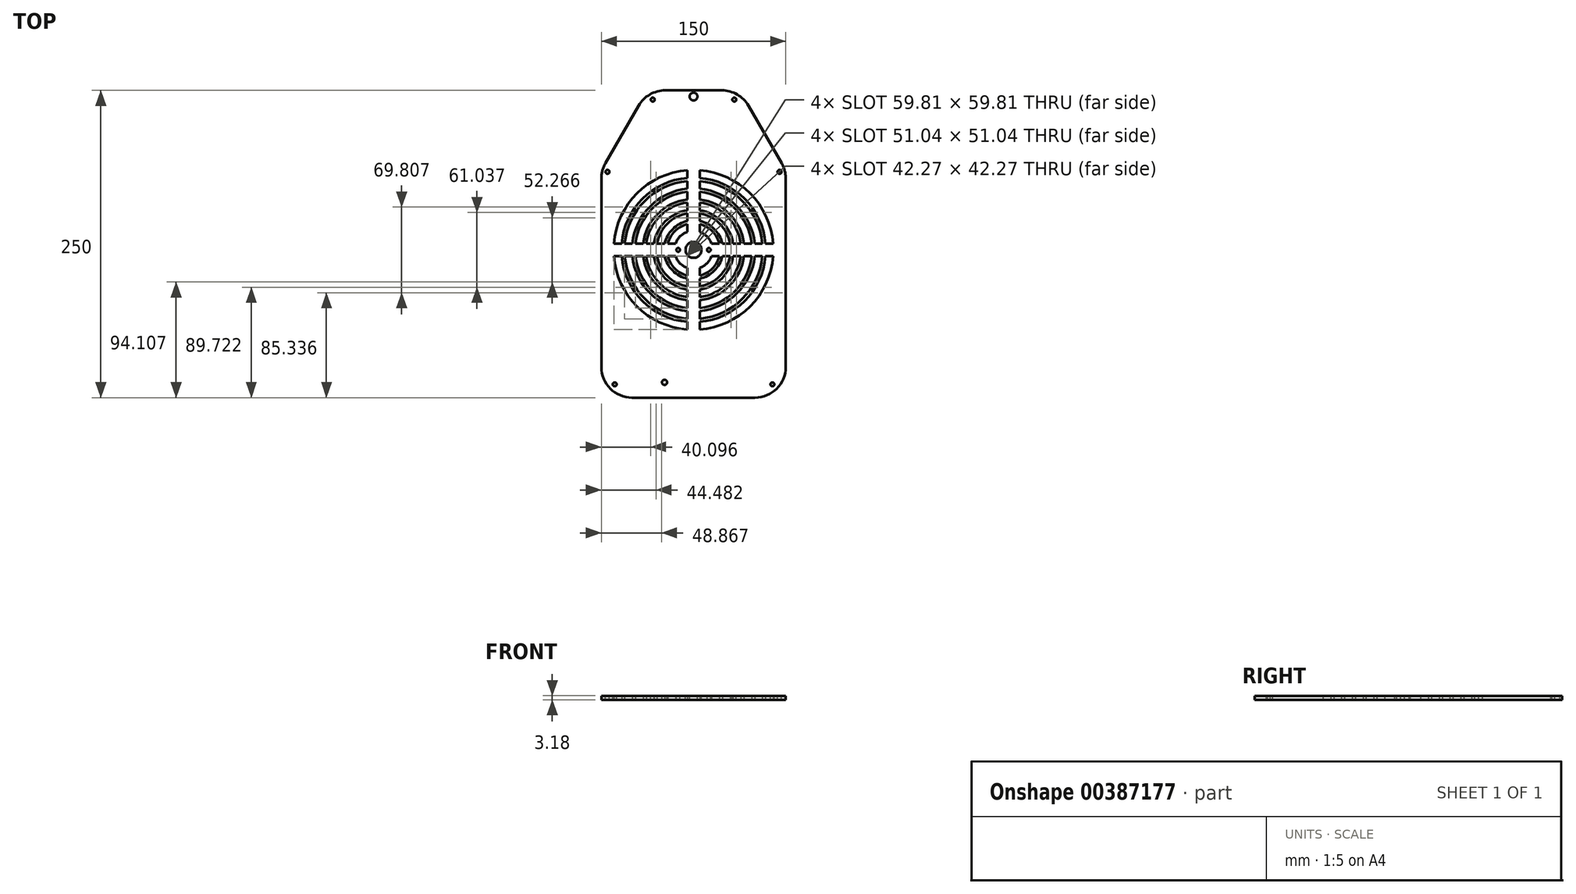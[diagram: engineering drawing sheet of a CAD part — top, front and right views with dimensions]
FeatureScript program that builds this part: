
annotation { "Feature Type Name" : "Feature", "Feature Type Description" : "" }
export const myFeature = defineFeature(function(context is Context, id is Id, definition is map)
    precondition{}
    {
        {
            var Q0;
            Q0=qCreatedBy(makeId("Top.planeOp"),FACE);
            var sketch = newSketch(context, id + "F0", { "sketchPlane" : qUnion([Q0])});
            skLineSegment(sketch, "E0", {"start": v(-75, -120.24) * mm, "end": v(75, -120.24) * mm});
            skLineSegment(sketch, "E1", {"start": v(75, -120.24) * mm, "end": v(75, 64.8) * mm});
            skLineSegment(sketch, "E2", {"start": v(75, 64.8) * mm, "end": v(37.5, 129.76) * mm});
            skLineSegment(sketch, "E3", {"start": v(37.5, 129.76) * mm, "end": v(-37.5, 129.76) * mm});
            skLineSegment(sketch, "E4", {"start": v(-37.5, 129.76) * mm, "end": v(-75, 64.8) * mm});
            skLineSegment(sketch, "E5", {"start": v(-75, 64.8) * mm, "end": v(-75, -120.24) * mm});
            skArc(sketch, "E6", {"start": v(-5, 64.8) * mm, "mid": v(-45.96, 45.96) * mm, "end": v(-64.8, 5) * mm});
            skLineSegment(sketch, "E7", {"start": v(-5, 64.8) * mm, "end": v(-5, 58.54) * mm});
            skLineSegment(sketch, "E8", {"start": v(-23.45, 5) * mm, "end": v(-29.73, 5) * mm});
            skLineSegment(sketch, "E9", {"start": v(-64.8, -5) * mm, "end": v(-58.54, -5) * mm});
            skLineSegment(sketch, "E10", {"start": v(-5, -23.45) * mm, "end": v(-5, -29.73) * mm});
            skLineSegment(sketch, "E11", {"start": v(5, -64.8) * mm, "end": v(5, -58.54) * mm});
            skLineSegment(sketch, "E12", {"start": v(23.45, -5) * mm, "end": v(29.73, -5) * mm});
            skLineSegment(sketch, "E13", {"start": v(64.8, 5) * mm, "end": v(58.54, 5) * mm});
            skLineSegment(sketch, "E14", {"start": v(5, 23.45) * mm, "end": v(5, 29.73) * mm});
            skArc(sketch, "E15.trimOffspring", {"start": v(64.8, 5) * mm, "mid": v(45.96, 45.96) * mm, "end": v(5, 64.8) * mm});
            skArc(sketch, "E16.trimOffspring", {"start": v(5, -64.8) * mm, "mid": v(45.96, -45.96) * mm, "end": v(64.8, -5) * mm});
            skArc(sketch, "E17.trimOffspring", {"start": v(-64.8, -5) * mm, "mid": v(-45.96, -45.96) * mm, "end": v(-5, -64.8) * mm});
            skPoint(sketch, "E18.visualSharp", {"position": v(-75, -120.24) * mm});
            skPoint(sketch, "E19.visualSharp", {"position": v(75, -120.24) * mm});
            skArc(sketch, "E20", {"start": v(-5, 23.45) * mm, "mid": v(-16.96, 16.96) * mm, "end": v(-23.45, 5) * mm});
            skArc(sketch, "E21.trimOffspring", {"start": v(-23.45, -5) * mm, "mid": v(-16.96, -16.96) * mm, "end": v(-5, -23.45) * mm});
            skArc(sketch, "E22.trimOffspring", {"start": v(23.45, 5) * mm, "mid": v(16.96, 16.96) * mm, "end": v(5, 23.45) * mm});
            skArc(sketch, "E23.trimOffspring", {"start": v(5, -23.45) * mm, "mid": v(16.96, -16.96) * mm, "end": v(23.45, -5) * mm});
            skLineSegment(sketch, "E24", {"start": v(0, 129.76) * mm, "end": v(0, -120.24) * mm, "construction": true});
            skArc(sketch, "E25", {"start": v(58.54, 5) * mm, "mid": v(41.54, 41.54) * mm, "end": v(5, 58.54) * mm});
            skArc(sketch, "E26", {"start": v(-56.04, -5) * mm, "mid": v(-39.78, -39.78) * mm, "end": v(-5, -56.04) * mm});
            skArc(sketch, "E27", {"start": v(-5, 49.77) * mm, "mid": v(-35.37, 35.37) * mm, "end": v(-49.77, 5) * mm});
            skArc(sketch, "E28", {"start": v(-5, 47.27) * mm, "mid": v(-33.6, 33.6) * mm, "end": v(-47.27, 5) * mm});
            skLineSegment(sketch, "E29.trimOffspring", {"start": v(-5, 56.04) * mm, "end": v(-5, 49.77) * mm});
            skLineSegment(sketch, "E30.trimOffspring", {"start": v(5, 58.54) * mm, "end": v(5, 64.8) * mm});
            skLineSegment(sketch, "E31.trimOffspring", {"start": v(-58.54, 5) * mm, "end": v(-64.8, 5) * mm});
            skLineSegment(sketch, "E32.trimOffspring", {"start": v(-56.04, -5) * mm, "end": v(-49.77, -5) * mm});
            skLineSegment(sketch, "E33.trimOffspring", {"start": v(-5, -58.54) * mm, "end": v(-5, -64.8) * mm});
            skLineSegment(sketch, "E34.trimOffspring", {"start": v(5, -56.04) * mm, "end": v(5, -49.77) * mm});
            skLineSegment(sketch, "E35.trimOffspring", {"start": v(58.54, -5) * mm, "end": v(64.8, -5) * mm});
            skLineSegment(sketch, "E36.trimOffspring", {"start": v(56.04, 5) * mm, "end": v(49.77, 5) * mm});
            skArc(sketch, "E37.trimOffspring", {"start": v(-58.54, -5) * mm, "mid": v(-41.54, -41.54) * mm, "end": v(-5, -58.54) * mm});
            skArc(sketch, "E38.trimOffspring", {"start": v(-5, 58.54) * mm, "mid": v(-41.54, 41.54) * mm, "end": v(-58.54, 5) * mm});
            skArc(sketch, "E39.trimOffspring", {"start": v(-5, 56.04) * mm, "mid": v(-39.78, 39.78) * mm, "end": v(-56.04, 5) * mm});
            skLineSegment(sketch, "E40.trimOffspring", {"start": v(-5, 47.27) * mm, "end": v(-5, 41) * mm});
            skLineSegment(sketch, "E41.trimOffspring", {"start": v(-49.77, 5) * mm, "end": v(-56.04, 5) * mm});
            skArc(sketch, "E42.trimOffspring", {"start": v(-49.77, -5) * mm, "mid": v(-35.37, -35.37) * mm, "end": v(-5, -49.77) * mm});
            skArc(sketch, "E43.trimOffspring", {"start": v(-47.27, -5) * mm, "mid": v(-33.6, -33.6) * mm, "end": v(-5, -47.27) * mm});
            skLineSegment(sketch, "E44.trimOffspring", {"start": v(-47.27, -5) * mm, "end": v(-41, -5) * mm});
            skLineSegment(sketch, "E45.trimOffspring", {"start": v(47.27, 5) * mm, "end": v(41, 5) * mm});
            skArc(sketch, "E46.trimOffspring", {"start": v(49.77, 5) * mm, "mid": v(35.37, 35.37) * mm, "end": v(5, 49.77) * mm});
            skArc(sketch, "E47.trimOffspring", {"start": v(47.27, 5) * mm, "mid": v(33.6, 33.6) * mm, "end": v(5, 47.27) * mm});
            skArc(sketch, "E48.trimOffspring", {"start": v(56.04, 5) * mm, "mid": v(39.78, 39.78) * mm, "end": v(5, 56.04) * mm});
            skLineSegment(sketch, "E49.trimOffspring", {"start": v(-5, -49.77) * mm, "end": v(-5, -56.04) * mm});
            skArc(sketch, "E50.trimOffspring", {"start": v(5, -47.27) * mm, "mid": v(33.6, -33.6) * mm, "end": v(47.27, -5) * mm});
            skArc(sketch, "E51.trimOffspring", {"start": v(5, -49.77) * mm, "mid": v(35.37, -35.37) * mm, "end": v(49.77, -5) * mm});
            skArc(sketch, "E52.trimOffspring", {"start": v(5, -56.04) * mm, "mid": v(39.78, -39.78) * mm, "end": v(56.04, -5) * mm});
            skLineSegment(sketch, "E53.trimOffspring", {"start": v(5, -47.27) * mm, "end": v(5, -41) * mm});
            skArc(sketch, "E54.trimOffspring", {"start": v(5, -58.54) * mm, "mid": v(41.54, -41.54) * mm, "end": v(58.54, -5) * mm});
            skLineSegment(sketch, "E55.trimOffspring", {"start": v(49.77, -5) * mm, "end": v(56.04, -5) * mm});
            skLineSegment(sketch, "E56.trimOffspring", {"start": v(5, 49.77) * mm, "end": v(5, 56.04) * mm});
            skArc(sketch, "E57", {"start": v(-5, 41) * mm, "mid": v(-29.2, 29.2) * mm, "end": v(-41, 5) * mm});
            skArc(sketch, "E58", {"start": v(-5, 29.73) * mm, "mid": v(-21.31, 21.31) * mm, "end": v(-29.73, 5) * mm});
            skArc(sketch, "E59.trimOffspring", {"start": v(-29.73, -5) * mm, "mid": v(-21.31, -21.31) * mm, "end": v(-5, -29.73) * mm});
            skArc(sketch, "E60.trimOffspring", {"start": v(-41, -5) * mm, "mid": v(-29.2, -29.2) * mm, "end": v(-5, -41) * mm});
            skArc(sketch, "E61.trimOffspring", {"start": v(5, -29.73) * mm, "mid": v(21.31, -21.31) * mm, "end": v(29.73, -5) * mm});
            skArc(sketch, "E62.trimOffspring", {"start": v(5, -41) * mm, "mid": v(29.2, -29.2) * mm, "end": v(41, -5) * mm});
            skArc(sketch, "E63.trimOffspring", {"start": v(29.73, 5) * mm, "mid": v(21.31, 21.31) * mm, "end": v(5, 29.73) * mm});
            skArc(sketch, "E64.trimOffspring", {"start": v(41, 5) * mm, "mid": v(29.2, 29.2) * mm, "end": v(5, 41) * mm});
            skLineSegment(sketch, "E65.trimOffspring", {"start": v(-5, 29.73) * mm, "end": v(-5, 23.45) * mm});
            skLineSegment(sketch, "E66.trimOffspring", {"start": v(5, 41) * mm, "end": v(5, 47.27) * mm});
            skLineSegment(sketch, "E67.trimOffspring", {"start": v(29.73, 5) * mm, "end": v(23.45, 5) * mm});
            skLineSegment(sketch, "E68.trimOffspring", {"start": v(41, -5) * mm, "end": v(47.27, -5) * mm});
            skLineSegment(sketch, "E69.trimOffspring", {"start": v(5, -29.73) * mm, "end": v(5, -23.45) * mm});
            skLineSegment(sketch, "E70.trimOffspring", {"start": v(-5, -41) * mm, "end": v(-5, -47.27) * mm});
            skLineSegment(sketch, "E71.trimOffspring", {"start": v(-29.73, -5) * mm, "end": v(-23.45, -5) * mm});
            skLineSegment(sketch, "E72.trimOffspring", {"start": v(-41, 5) * mm, "end": v(-47.27, 5) * mm});
            skArc(sketch, "E73", {"start": v(-5, 38.5) * mm, "mid": v(-27.45, 27.45) * mm, "end": v(-38.5, 5) * mm});
            skArc(sketch, "E74", {"start": v(-5, 32.23) * mm, "mid": v(-23.06, 23.06) * mm, "end": v(-32.23, 5) * mm});
            skLineSegment(sketch, "E75", {"start": v(-5, 32.23) * mm, "end": v(-5, 38.5) * mm});
            skLineSegment(sketch, "E76", {"start": v(5, 32.23) * mm, "end": v(5, 38.5) * mm});
            skLineSegment(sketch, "E77", {"start": v(32.23, 5) * mm, "end": v(38.5, 5) * mm});
            skLineSegment(sketch, "E78", {"start": v(32.23, -5) * mm, "end": v(38.5, -5) * mm});
            skLineSegment(sketch, "E79", {"start": v(-32.23, -5) * mm, "end": v(-38.5, -5) * mm});
            skLineSegment(sketch, "E80", {"start": v(-32.23, 5) * mm, "end": v(-38.5, 5) * mm});
            skArc(sketch, "E81.trimOffspring", {"start": v(32.23, 5) * mm, "mid": v(23.06, 23.06) * mm, "end": v(5, 32.23) * mm});
            skArc(sketch, "E82.trimOffspring", {"start": v(38.5, 5) * mm, "mid": v(27.45, 27.45) * mm, "end": v(5, 38.5) * mm});
            skArc(sketch, "E83.trimOffspring", {"start": v(-32.23, -5) * mm, "mid": v(-23.06, -23.06) * mm, "end": v(-5, -32.23) * mm});
            skArc(sketch, "E84.trimOffspring", {"start": v(-38.5, -5) * mm, "mid": v(-27.45, -27.45) * mm, "end": v(-5, -38.5) * mm});
            skLineSegment(sketch, "E85", {"start": v(-5, -32.23) * mm, "end": v(-5, -38.5) * mm});
            skLineSegment(sketch, "E86", {"start": v(5, -38.5) * mm, "end": v(5, -32.23) * mm});
            skArc(sketch, "E87.trimOffspring", {"start": v(5, -32.23) * mm, "mid": v(23.06, -23.06) * mm, "end": v(32.23, -5) * mm});
            skArc(sketch, "E88.trimOffspring", {"start": v(5, -38.5) * mm, "mid": v(27.45, -27.45) * mm, "end": v(38.5, -5) * mm});
            skPoint(sketch, "E89", {"position": v(-26.59, -5) * mm});
            skArc(sketch, "E90", {"start": v(-20.95, -5) * mm, "mid": v(-15.23, -15.23) * mm, "end": v(-5, -20.95) * mm});
            skArc(sketch, "E91", {"start": v(-14.68, -5) * mm, "mid": v(-10.97, -10.97) * mm, "end": v(-5, -14.68) * mm});
            skLineSegment(sketch, "E92", {"start": v(-5, 20.95) * mm, "end": v(-5, 14.68) * mm});
            skLineSegment(sketch, "E93", {"start": v(-20.95, 5) * mm, "end": v(-14.68, 5) * mm});
            skLineSegment(sketch, "E94", {"start": v(-20.95, -5) * mm, "end": v(-14.68, -5) * mm});
            skLineSegment(sketch, "E95", {"start": v(5, 20.95) * mm, "end": v(5, 14.68) * mm});
            skLineSegment(sketch, "E96", {"start": v(20.95, 5) * mm, "end": v(14.68, 5) * mm});
            skLineSegment(sketch, "E97", {"start": v(20.95, -5) * mm, "end": v(14.68, -5) * mm});
            skLineSegment(sketch, "E98", {"start": v(-5, -20.95) * mm, "end": v(-5, -14.68) * mm});
            skLineSegment(sketch, "E99", {"start": v(5, -14.68) * mm, "end": v(5, -20.95) * mm});
            skArc(sketch, "E100.trimOffspring", {"start": v(-5, 14.68) * mm, "mid": v(-10.97, 10.97) * mm, "end": v(-14.68, 5) * mm});
            skArc(sketch, "E101.trimOffspring", {"start": v(-5, 20.95) * mm, "mid": v(-15.23, 15.23) * mm, "end": v(-20.95, 5) * mm});
            skArc(sketch, "E102.trimOffspring", {"start": v(14.68, 5) * mm, "mid": v(10.97, 10.97) * mm, "end": v(5, 14.68) * mm});
            skArc(sketch, "E103.trimOffspring", {"start": v(20.95, 5) * mm, "mid": v(15.23, 15.23) * mm, "end": v(5, 20.95) * mm});
            skArc(sketch, "E104.trimOffspring", {"start": v(5, -14.68) * mm, "mid": v(10.97, -10.97) * mm, "end": v(14.68, -5) * mm});
            skArc(sketch, "E105.trimOffspring", {"start": v(5, -20.95) * mm, "mid": v(15.23, -15.23) * mm, "end": v(20.95, -5) * mm});
            skSolve(sketch);
        }
        {
            var Q0;
            Q0=makeQuery(id+"F0.imprint","IMPRINT",FACE,{"disambiguationData":[TD([[makeQuery(id+"F0.imprint","IMPRINT",EDGE,{"derivedFrom":sQuery(id+"F0.wireOp",EDGE,"E0")}),1.0]])]});
            extrude(context, id + "F1", {"entities" : qUnion([Q0]), "depth" : 3.17 * mm});
        }
        {
            var Q0;
            Q0=makeQuery(id+"F1.opExtrude","CAP_FACE",FACE,{"disambiguationData":[OSD([sQuery(id+"F0.wireOp",EDGE,"E0"),sQuery(id+"F0.wireOp",EDGE,"E1"),sQuery(id+"F0.wireOp",EDGE,"E2"),sQuery(id+"F0.wireOp",EDGE,"E3"),sQuery(id+"F0.wireOp",EDGE,"E4"),sQuery(id+"F0.wireOp",EDGE,"E5"),sQuery(id+"F0.wireOp",EDGE,"E6"),sQuery(id+"F0.wireOp",EDGE,"E7"),sQuery(id+"F0.wireOp",EDGE,"E8"),sQuery(id+"F0.wireOp",EDGE,"E9"),sQuery(id+"F0.wireOp",EDGE,"E10"),sQuery(id+"F0.wireOp",EDGE,"E11"),sQuery(id+"F0.wireOp",EDGE,"E12"),sQuery(id+"F0.wireOp",EDGE,"E13"),sQuery(id+"F0.wireOp",EDGE,"E14"),sQuery(id+"F0.wireOp",EDGE,"E15.trimOffspring"),sQuery(id+"F0.wireOp",EDGE,"E16.trimOffspring"),sQuery(id+"F0.wireOp",EDGE,"E17.trimOffspring"),sQuery(id+"F0.wireOp",EDGE,"E18.filletArc"),sQuery(id+"F0.wireOp",EDGE,"E19.filletArc")])],"isStart":false});
            var sketch = newSketch(context, id + "F2", { "sketchPlane" : qUnion([Q0])});
            skLineSegment(sketch, "E106.bottom", {"start": v(-25, -120.24) * mm, "end": v(25, -120.24) * mm, "construction": true});
            skLineSegment(sketch, "E106.top", {"start": v(-25, -95.24) * mm, "end": v(25, -95.24) * mm, "construction": true});
            skLineSegment(sketch, "E106.left", {"start": v(-25, -120.24) * mm, "end": v(-25, -95.24) * mm, "construction": true});
            skLineSegment(sketch, "E106.right", {"start": v(25, -120.24) * mm, "end": v(25, -95.24) * mm, "construction": true});
            skArc(sketch, "E107", {"start": v(-20.52, -102.2) * mm, "mid": v(-21.8, -99.51) * mm, "end": v(-24.48, -100.78) * mm});
            skArc(sketch, "E108", {"start": v(-24.48, -114.7) * mm, "mid": v(-21.8, -115.97) * mm, "end": v(-20.52, -113.28) * mm});
            skArc(sketch, "E109", {"start": v(20.52, -113.28) * mm, "mid": v(21.8, -115.97) * mm, "end": v(24.48, -114.7) * mm, "construction": true});
            skArc(sketch, "E110", {"start": v(24.48, -100.78) * mm, "mid": v(21.8, -99.51) * mm, "end": v(20.52, -102.2) * mm, "construction": true});
            skCircle(sketch, "E111", {"center": v(0, 124.76) * mm, "radius": 3.18 * mm});
            skCircle(sketch, "E112", {"center": v(0, 0) * mm, "radius": 6.5 * mm});
            skArc(sketch, "E113", {"start": v(-20.52, -102.2) * mm, "mid": v(-21.8, -99.51) * mm, "end": v(-24.48, -100.78) * mm, "construction": true});
            skArc(sketch, "E114", {"start": v(-24.48, -114.7) * mm, "mid": v(-21.8, -115.97) * mm, "end": v(-20.52, -113.28) * mm, "construction": true});
            skArc(sketch, "E115", {"start": v(-24.48, -100.78) * mm, "mid": v(-25.68, -107.74) * mm, "end": v(-24.48, -114.7) * mm, "construction": true});
            skArc(sketch, "E116", {"start": v(-20.52, -102.2) * mm, "mid": v(-21.48, -107.74) * mm, "end": v(-20.52, -113.28) * mm, "construction": true});
            skArc(sketch, "E117.MirrorCS", {"start": v(20.52, -102.2) * mm, "mid": v(21.48, -107.74) * mm, "end": v(20.52, -113.28) * mm, "construction": true});
            skArc(sketch, "E118.MirrorCS", {"start": v(24.48, -100.78) * mm, "mid": v(25.68, -107.74) * mm, "end": v(24.48, -114.7) * mm, "construction": true});
            skArc(sketch, "E119.MirrorCS", {"start": v(20.52, -102.2) * mm, "mid": v(21.8, -99.51) * mm, "end": v(24.48, -100.78) * mm, "construction": true});
            skArc(sketch, "E120.MirrorCS", {"start": v(24.48, -114.7) * mm, "mid": v(21.8, -115.97) * mm, "end": v(20.52, -113.28) * mm, "construction": true});
            skArc(sketch, "E121", {"start": v(-22.5, -101.5) * mm, "mid": v(-23.58, -107.74) * mm, "end": v(-22.5, -114) * mm, "construction": true});
            skCircle(sketch, "E122", {"center": v(-23.58, -107.74) * mm, "radius": 2.1 * mm});
            skCircle(sketch, "E123.MirrorC", {"center": v(23.58, -107.74) * mm, "radius": 2.1 * mm});
            skCircle(sketch, "E124", {"center": v(-12.5, 0) * mm, "radius": 1.5 * mm});
            skCircle(sketch, "E125", {"center": v(12.5, 0) * mm, "radius": 1.5 * mm});
            skLineSegment(sketch, "E126", {"start": v(-12.5, 0) * mm, "end": v(12.5, 0) * mm, "construction": true});
            skSolve(sketch);
        }
        {
            var Q0;
            Q0=makeQuery(id+"F2.imprint","IMPRINT",FACE,{"disambiguationData":[TD([[makeQuery(id+"F2.imprint","IMPRINT",EDGE,{"derivedFrom":sQuery(id+"F2.wireOp",EDGE,"E109")}),1.0]])]});
            var Q1;
            Q1=makeQuery(id+"F2.imprint","IMPRINT",FACE,{"disambiguationData":[TD([[makeQuery(id+"F2.imprint","IMPRINT",EDGE,{"derivedFrom":sQuery(id+"F2.wireOp",EDGE,"E110")}),1.0]])]});
            var Q2;
            Q2=makeQuery(id+"F2.imprint","IMPRINT",FACE,{"disambiguationData":[TD([[makeQuery(id+"F2.imprint","IMPRINT",EDGE,{"derivedFrom":sQuery(id+"F2.wireOp",EDGE,"E107")}),1.0]])]});
            var Q3;
            Q3=makeQuery(id+"F2.imprint","IMPRINT",FACE,{"disambiguationData":[TD([[makeQuery(id+"F2.imprint","IMPRINT",EDGE,{"derivedFrom":sQuery(id+"F2.wireOp",EDGE,"E108")}),1.0]])]});
            var Q4;
            Q4=makeQuery(id+"F2.imprint","IMPRINT",FACE,{"disambiguationData":[TD([[makeQuery(id+"F2.imprint","IMPRINT",EDGE,{"derivedFrom":sQuery(id+"F2.wireOp",EDGE,"E111")}),1.0]])]});
            var Q5;
            Q5=makeQuery(id+"F2.imprint","IMPRINT",FACE,{"disambiguationData":[TD([[makeQuery(id+"F2.imprint","IMPRINT",EDGE,{"derivedFrom":sQuery(id+"F2.wireOp",EDGE,"E113")}),1.0]])]});
            var Q6;
            Q6=makeQuery(id+"F2.imprint","IMPRINT",FACE,{"disambiguationData":[TD([[makeQuery(id+"F2.imprint","IMPRINT",EDGE,{"derivedFrom":sQuery(id+"F2.wireOp",EDGE,"E117.MirrorCS")}),1.0]])]});
            var Q7;
            Q7=makeQuery(id+"F2.imprint","IMPRINT",FACE,{"disambiguationData":[TD([[makeQuery(id+"F2.imprint","IMPRINT",EDGE,{"derivedFrom":sQuery(id+"F2.wireOp",EDGE,"E112")}),1.0]])]});
            var Q8;
            Q8=makeQuery(id+"F2.imprint","IMPRINT",FACE,{"disambiguationData":[TD([[makeQuery(id+"F2.imprint","IMPRINT",EDGE,{"derivedFrom":sQuery(id+"F2.wireOp",EDGE,"E122")}),1.0]])]});
            var Q9;
            Q9=makeQuery(id+"F2.imprint","IMPRINT",FACE,{"disambiguationData":[TD([[makeQuery(id+"F2.imprint","IMPRINT",EDGE,{"derivedFrom":sQuery(id+"F2.wireOp",EDGE,"E123.MirrorC")}),-1.0]])]});
            var Q10;
            Q10=makeQuery(id+"F2.imprint","IMPRINT",FACE,{"disambiguationData":[TD([[makeQuery(id+"F2.imprint","IMPRINT",EDGE,{"derivedFrom":sQuery(id+"F2.wireOp",EDGE,"E124")}),1.0]])]});
            var Q11;
            Q11=makeQuery(id+"F2.imprint","IMPRINT",FACE,{"disambiguationData":[TD([[makeQuery(id+"F2.imprint","IMPRINT",EDGE,{"derivedFrom":sQuery(id+"F2.wireOp",EDGE,"E125")}),1.0]])]});
            extrude(context, id + "F3", {"entities" : qUnion([Q0, Q1, Q2, Q3, Q4, Q5, Q6, Q7, Q8, Q9, Q10, Q11]), "operationType" : NewBodyOperationType.REMOVE, "endBound" : BoundingType.THROUGH_ALL, "oppositeDirection" : true, "depth" : 25 * mm});
        }
        {
            var Q0;
            Q0=makeQuery(id+"F1.opExtrude","SWEPT_EDGE",EDGE,{"disambiguationData":[OSD([sQuery(id+"F0.wireOp",EDGE,"E0"),sQuery(id+"F0.wireOp",EDGE,"E5")])]});
            var Q1;
            Q1=makeQuery(id+"F1.opExtrude","SWEPT_EDGE",EDGE,{"disambiguationData":[OSD([sQuery(id+"F0.wireOp",EDGE,"E0"),sQuery(id+"F0.wireOp",EDGE,"E1")])]});
            var Q2;
            Q2=makeQuery(id+"F1.opExtrude","SWEPT_EDGE",EDGE,{"disambiguationData":[OSD([sQuery(id+"F0.wireOp",EDGE,"E3"),sQuery(id+"F0.wireOp",EDGE,"E4")])]});
            var Q3;
            Q3=makeQuery(id+"F1.opExtrude","SWEPT_EDGE",EDGE,{"disambiguationData":[OSD([sQuery(id+"F0.wireOp",EDGE,"E4"),sQuery(id+"F0.wireOp",EDGE,"E5")])]});
            var Q4;
            Q4=makeQuery(id+"F1.opExtrude","SWEPT_EDGE",EDGE,{"disambiguationData":[OSD([sQuery(id+"F0.wireOp",EDGE,"E1"),sQuery(id+"F0.wireOp",EDGE,"E2")])]});
            var Q5;
            Q5=makeQuery(id+"F1.opExtrude","SWEPT_EDGE",EDGE,{"disambiguationData":[OSD([sQuery(id+"F0.wireOp",EDGE,"E2"),sQuery(id+"F0.wireOp",EDGE,"E3")])]});
            fillet(context, id + "F4", {"entities" : qUnion([Q0, Q1, Q2, Q3, Q4, Q5]), "radius" : 25 * mm, "tangentPropagation" : true, "allowEdgeOverflow" : false});
        }
        {
            var Q0;
            Q0=makeQuery(id+"F1.opExtrude","CAP_FACE",FACE,{"disambiguationData":[OSD([sQuery(id+"F0.wireOp",EDGE,"E0"),sQuery(id+"F0.wireOp",EDGE,"E1"),sQuery(id+"F0.wireOp",EDGE,"E2"),sQuery(id+"F0.wireOp",EDGE,"E3"),sQuery(id+"F0.wireOp",EDGE,"E4"),sQuery(id+"F0.wireOp",EDGE,"E5"),sQuery(id+"F0.wireOp",EDGE,"E6"),sQuery(id+"F0.wireOp",EDGE,"E7"),sQuery(id+"F0.wireOp",EDGE,"E8"),sQuery(id+"F0.wireOp",EDGE,"E9"),sQuery(id+"F0.wireOp",EDGE,"E10"),sQuery(id+"F0.wireOp",EDGE,"E11"),sQuery(id+"F0.wireOp",EDGE,"E12"),sQuery(id+"F0.wireOp",EDGE,"E13"),sQuery(id+"F0.wireOp",EDGE,"E14"),sQuery(id+"F0.wireOp",EDGE,"E15.trimOffspring"),sQuery(id+"F0.wireOp",EDGE,"E16.trimOffspring"),sQuery(id+"F0.wireOp",EDGE,"E17.trimOffspring"),sQuery(id+"F0.wireOp",EDGE,"E20"),sQuery(id+"F0.wireOp",EDGE,"E21.trimOffspring"),sQuery(id+"F0.wireOp",EDGE,"E22.trimOffspring"),sQuery(id+"F0.wireOp",EDGE,"E23.trimOffspring")])],"isStart":false});
            var sketch = newSketch(context, id + "F5", { "sketchPlane" : qUnion([Q0])});
            skCircle(sketch, "E127", {"center": v(-64.14, -109.38) * mm, "radius": 1.59 * mm});
            skCircle(sketch, "E128", {"center": v(64.14, -109.38) * mm, "radius": 1.59 * mm});
            skCircle(sketch, "E129", {"center": v(70, 63.47) * mm, "radius": 1.59 * mm});
            skCircle(sketch, "E130", {"center": v(-70, 63.47) * mm, "radius": 1.59 * mm});
            skCircle(sketch, "E131", {"center": v(33.17, 122.26) * mm, "radius": 1.59 * mm});
            skCircle(sketch, "E132", {"center": v(-33.17, 122.26) * mm, "radius": 1.59 * mm});
            skLineSegment(sketch, "E133", {"start": v(-64.14, -109.38) * mm, "end": v(-67.68, -112.92) * mm, "construction": true});
            skLineSegment(sketch, "E134", {"start": v(64.14, -109.38) * mm, "end": v(67.68, -112.92) * mm, "construction": true});
            skSolve(sketch);
        }
        {
            var Q0;
            Q0=makeQuery(id+"F5.imprint","IMPRINT",FACE,{"disambiguationData":[TD([[makeQuery(id+"F5.imprint","IMPRINT",EDGE,{"derivedFrom":sQuery(id+"F5.wireOp",EDGE,"E132")}),1.0]])]});
            var Q1;
            Q1=makeQuery(id+"F5.imprint","IMPRINT",FACE,{"disambiguationData":[TD([[makeQuery(id+"F5.imprint","IMPRINT",EDGE,{"derivedFrom":sQuery(id+"F5.wireOp",EDGE,"E131")}),1.0]])]});
            var Q2;
            Q2=makeQuery(id+"F5.imprint","IMPRINT",FACE,{"disambiguationData":[TD([[makeQuery(id+"F5.imprint","IMPRINT",EDGE,{"derivedFrom":sQuery(id+"F5.wireOp",EDGE,"E129")}),1.0]])]});
            var Q3;
            Q3=makeQuery(id+"F5.imprint","IMPRINT",FACE,{"disambiguationData":[TD([[makeQuery(id+"F5.imprint","IMPRINT",EDGE,{"derivedFrom":sQuery(id+"F5.wireOp",EDGE,"E130")}),1.0]])]});
            var Q4;
            Q4=makeQuery(id+"F5.imprint","IMPRINT",FACE,{"disambiguationData":[TD([[makeQuery(id+"F5.imprint","IMPRINT",EDGE,{"derivedFrom":sQuery(id+"F5.wireOp",EDGE,"E127")}),1.0]])]});
            var Q5;
            Q5=makeQuery(id+"F5.imprint","IMPRINT",FACE,{"disambiguationData":[TD([[makeQuery(id+"F5.imprint","IMPRINT",EDGE,{"derivedFrom":sQuery(id+"F5.wireOp",EDGE,"E128")}),1.0]])]});
            extrude(context, id + "F6", {"entities" : qUnion([Q0, Q1, Q2, Q3, Q4, Q5]), "operationType" : NewBodyOperationType.REMOVE, "endBound" : BoundingType.THROUGH_ALL, "oppositeDirection" : true, "depth" : 25 * mm});
        }
    });
